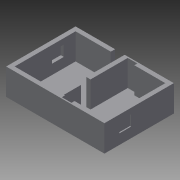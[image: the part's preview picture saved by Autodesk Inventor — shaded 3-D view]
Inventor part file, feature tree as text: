
AUTODESK INVENTOR PART (.ipt)
format: ipt  version: 2014 (Build 180170000, 170)  size: 235,008 bytes
history: native  units: in
note: dims shown in document units (in); Inventor stores cm internally (conversion verified against a paired STEP export)
features: extrude x8, sketch x8, projected_geometry x4
ambient origin geometry x8: Origin, YZ Plane, XZ Plane, XY Plane, X Axis, Y Axis, Z Axis, Center Point
bodies: Solid1 (feature_tree)
feature tree (20):
  extrude  "Extrusion1"  Depth=330.7087in
  extrude  "Extrusion2"  Depth=255.9055in
  extrude  "Extrusion3"  Depth=153.5433in
  extrude  "Extrusion4"  Depth=62.9921in
  extrude  "Extrusion5"  Depth=43.3071in
  extrude  "Extrusion8"  Depth=224.4094in
  extrude  "Pallets"  Depth=141.7323in
  extrude  "Instrumentation"  Depth=330.7087in
  sketch  "Sketch1"  dims[d0=362.2047in d1=255.9055in d2=330.7087in d3=224.4094in]
  sketch  "Sketch2"  dims[d4=110.2362in d5=35.4331in d6=255.9055in d7=224.4094in]
  projected_geometry  "Projected Loop1"
  sketch  "Sketch3"  dims[d8=114.1732in d10=153.5433in d11=35.4331in]
  projected_geometry  "Projected Loop2"
  projected_geometry  "Projected Loop3"
  sketch  "Sketch4"  dims[d12=15.748in d13=62.9921in]
  sketch  "Sketch5"  dims[d14=35.4331in d15=43.3071in]
  sketch  "Sketch6"  dims[d19=255.9055in d20=224.4094in]
  sketch  "Sketch7"  dims[d21=62.9921in d22=141.7323in]
  sketch  "Sketch8"  dims[d23=362.2047in d24=330.7087in d25=110.2362in d27=96.0in d28=0.0in d29=1.0in d30=0.0in d31=4.5in d33=4.5in d34=1.0in d35=0.0in d36=43.3071in d37=43.3071in d38=36.0in d39=39.3701in d40=11.25in d41=0.0in d42=39.3701in d43=43.3071in d44=39.3701in d45=36.0in d46=11.25in d47=0.0in d55=12.0in d56=11.811in d57=19.685in d58=12.0in d59=12.0in d60=12.0in d61=23.622in d62=23.622in d63=23.622in d64=23.622in d65=23.622in d66=23.622in d69=110.2362in d70=82.6772in d71=12.0in d72=12.0in d75=12.0in d76=12.0in d77=6.0in d78=0.0in d79=11.811in d80=7.874in d81=11.811in d82=47.2441in d83=39.3701in d84=47.2441in d85=6.0in d86=0.0in d87=6.0in d91=5.0in d92=10.0in d93=6.0in d94=3.937in d95=0.0in]
  projected_geometry  "Projected Loop4"
